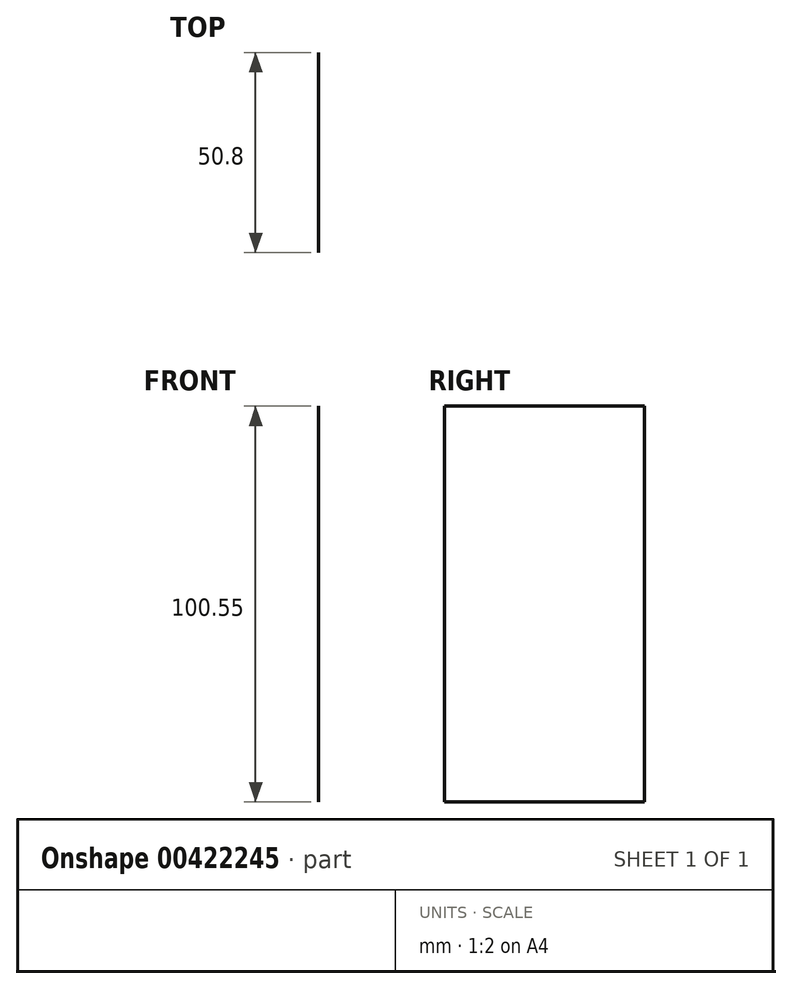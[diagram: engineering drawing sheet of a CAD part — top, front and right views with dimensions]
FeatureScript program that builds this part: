
annotation { "Feature Type Name" : "Feature", "Feature Type Description" : "" }
export const myFeature = defineFeature(function(context is Context, id is Id, definition is map)
    precondition{}
    {
        {
            var Q0;
            Q0=qCreatedBy(makeId("Front.planeOp"),FACE);
            var sketch = newSketch(context, id + "F0", { "sketchPlane" : qUnion([Q0])});
            skLineSegment(sketch, "E0.bottom", {"start": v(-52.1, 58.57) * mm, "end": v(54.52, 58.57) * mm});
            skLineSegment(sketch, "E0.top", {"start": v(-52.1, -41.98) * mm, "end": v(54.52, -41.98) * mm});
            skLineSegment(sketch, "E0.left", {"start": v(-52.1, 58.57) * mm, "end": v(-52.1, -41.98) * mm});
            skLineSegment(sketch, "E0.right", {"start": v(54.52, 58.57) * mm, "end": v(54.52, -41.98) * mm});
            skLineSegment(sketch, "E1", {"start": v(-15.88, 58.57) * mm, "end": v(-15.88, -41.98) * mm});
            skLineSegment(sketch, "E2", {"start": v(18.92, 58.57) * mm, "end": v(18.92, -41.98) * mm});
            skLineSegment(sketch, "E3", {"start": v(-52.1, 23.16) * mm, "end": v(54.52, 23.16) * mm});
            skLineSegment(sketch, "E4", {"start": v(-52.1, -10.42) * mm, "end": v(54.52, -10.42) * mm});
            skSolve(sketch);
        }
        {
            var Q0;
            Q0=sQuery(id+"F0.wireOp",EDGE,"E2");
            extrude(context, id + "F1", {"bodyType" : ToolBodyType.SURFACE, "operationType" : NewBodyOperationType.ADD, "surfaceEntities" : qUnion([Q0]), "depth" : 50.8 * mm, "offsetDistance" : 25.4 * mm});
        }
    });
